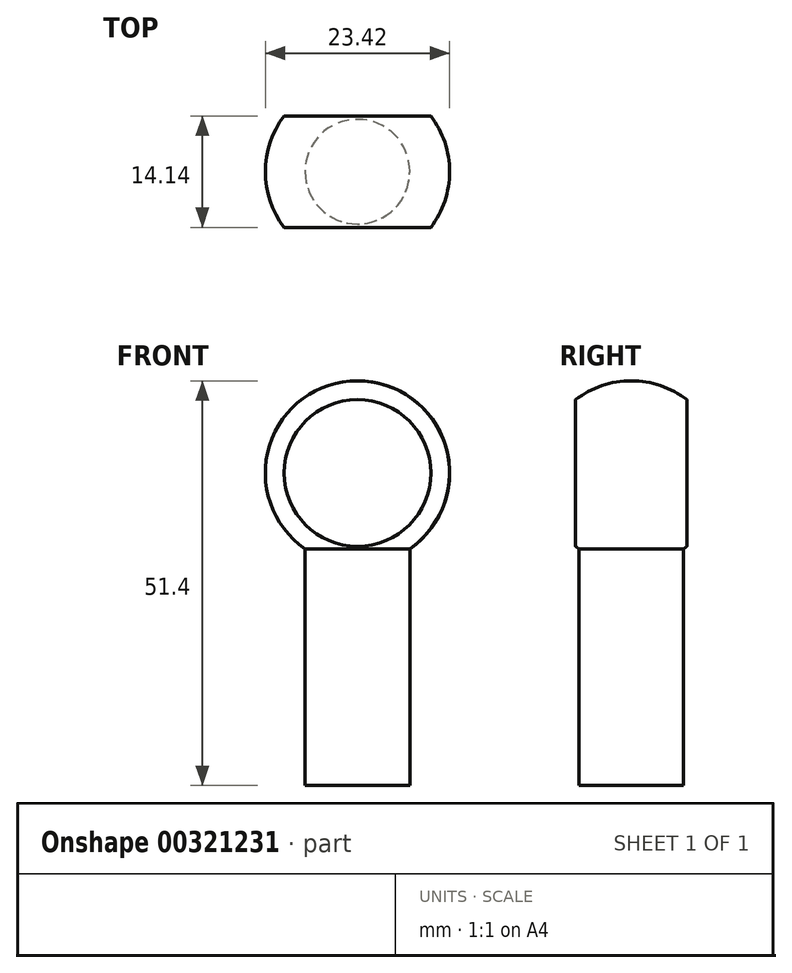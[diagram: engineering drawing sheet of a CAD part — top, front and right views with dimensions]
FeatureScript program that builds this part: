
annotation { "Feature Type Name" : "Feature", "Feature Type Description" : "" }
export const myFeature = defineFeature(function(context is Context, id is Id, definition is map)
    precondition{}
    {
        {
            var Q0;
            Q0=qCreatedBy(makeId("Front.planeOp"),FACE);
            var sketch = newSketch(context, id + "F0", { "sketchPlane" : qUnion([Q0])});
            skLineSegment(sketch, "E0", {"start": v(0, -16.96) * mm, "end": v(0, 0) * mm, "construction": true});
            skLineSegment(sketch, "E1", {"start": v(-6.65, 0) * mm, "end": v(-6.65, 30.06) * mm});
            skLineSegment(sketch, "E2", {"start": v(-6.65, 0) * mm, "end": v(0, 0) * mm});
            skLineSegment(sketch, "E3", {"start": v(0, 51.4) * mm, "end": v(0, 0) * mm});
            skArc(sketch, "E4", {"start": v(0, 51.4) * mm, "mid": v(-11.18, 43.18) * mm, "end": v(-6.65, 30.06) * mm});
            skSolve(sketch);
        }
        {
            var Q0;
            Q0=makeQuery(id+"F0.imprint","IMPRINT",FACE,{"disambiguationData":[TD([[makeQuery(id+"F0.imprint","IMPRINT",EDGE,{"derivedFrom":sQuery(id+"F0.wireOp",EDGE,"E1")}),-1.0]])]});
            var Q1;
            Q1=sQuery(id+"F0.wireOp",EDGE,"E0");
            revolve(context, id + "F1", {"entities" : qUnion([Q0]), "axis" : qUnion([Q1]), "revolveType" : RevolveType.FULL});
        }
        {
            var Q0;
            Q0=qCreatedBy(makeId("Top.planeOp"),FACE);
            cPlane(context, id + "F2", {"entities" : qUnion([Q0]), "cplaneType" : CPlaneType.OFFSET, "offset" : 30 * mm, "width" : 150 * mm, "height" : 150 * mm});
        }
        {
            var Q0;
            Q0=qCreatedBy(id+"F2.planeOp",FACE);
            var sketch = newSketch(context, id + "F3", { "sketchPlane" : qUnion([Q0])});
            skLineSegment(sketch, "E5.bottom", {"start": v(14.92, -7.07) * mm, "end": v(-14.92, -7.07) * mm});
            skLineSegment(sketch, "E5.top", {"start": v(14.92, 7.07) * mm, "end": v(-14.92, 7.07) * mm});
            skLineSegment(sketch, "E5.left", {"start": v(14.92, -7.07) * mm, "end": v(14.92, 7.07) * mm});
            skLineSegment(sketch, "E5.right", {"start": v(-14.92, -7.07) * mm, "end": v(-14.92, 7.07) * mm});
            skPoint(sketch, "E5.middle", {"position": v(0, 0) * mm});
            skSolve(sketch);
        }
        {
            var Q0;
            Q0 = qSketchRegion(id + "F3", true);
            extrude(context, id + "F4", {"entities" : qUnion([Q0]), "operationType" : NewBodyOperationType.INTERSECT, "endBound" : BoundingType.THROUGH_ALL, "depth" : 25 * mm, "hasSecondDirection" : true, "secondDirectionBound" : SecondDirectionBoundingType.THROUGH_ALL, "secondDirectionOppositeDirection" : true, "secondDirectionDepth" : 25 * mm});
        }
    });
